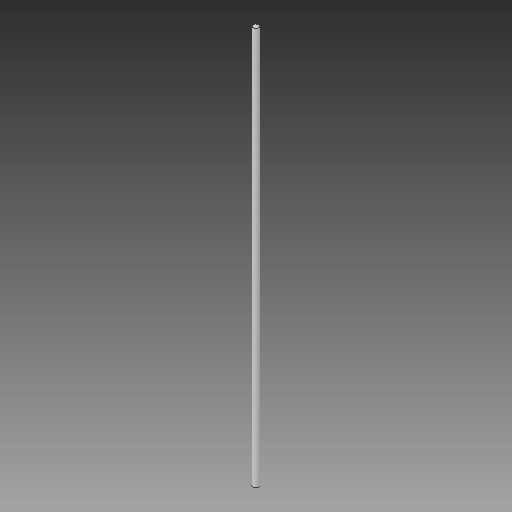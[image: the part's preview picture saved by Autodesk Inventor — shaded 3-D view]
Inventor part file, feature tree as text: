
AUTODESK INVENTOR PART (.ipt)
format: ipt  version: 2018 (Build 220112000, 112)  size: 70,144 bytes
history: native  units: mm
features: extrude x1, sketch x1
ambient origin geometry x8: Origin, YZ Plane, XZ Plane, XY Plane, X Axis, Y Axis, Z Axis, Center Point
bodies: Solid1 (feature_tree)
feature tree (2):
  extrude  "Extrusion1"  Depth=830.0mm TaperAngle=0.0deg
  sketch  "Sketch1"  dims[d0=12.0mm d1=830.0mm d2=0.0mm]
